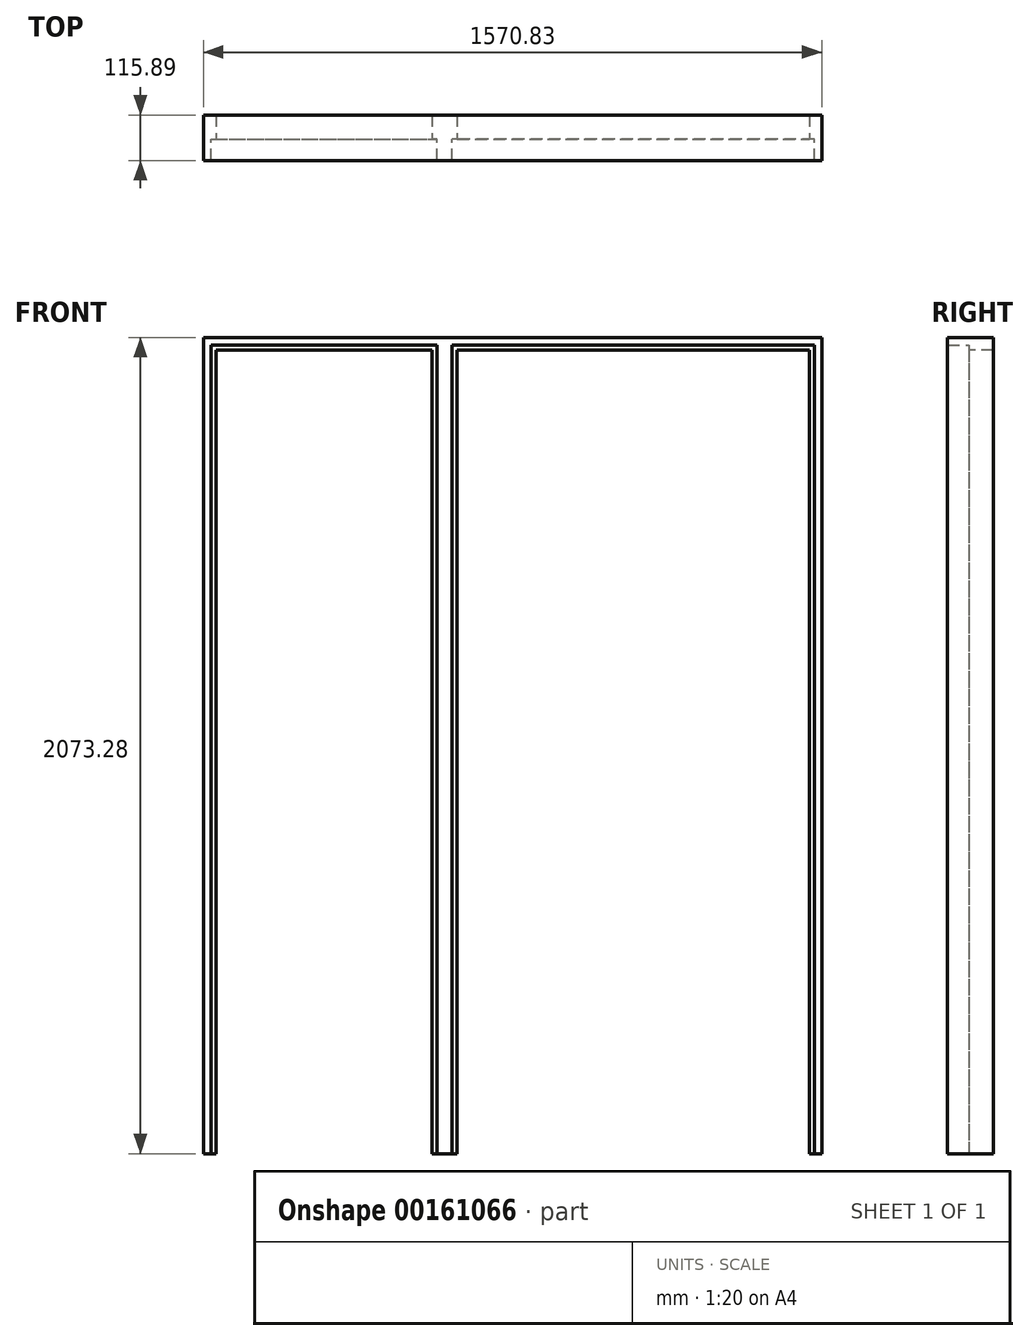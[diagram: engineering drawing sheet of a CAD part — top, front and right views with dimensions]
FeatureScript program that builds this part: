
annotation { "Feature Type Name" : "Feature", "Feature Type Description" : "" }
export const myFeature = defineFeature(function(context is Context, id is Id, definition is map)
    precondition{}
    {
        {
            var Q0;
            Q0=qCreatedBy(makeId("Front.planeOp"),FACE);
            cPlane(context, id + "F0", {"entities" : qUnion([Q0]), "cplaneType" : CPlaneType.OFFSET, "offset" : 3.17 * mm, "oppositeDirection" : true, "width" : 152.4 * mm, "height" : 152.4 * mm});
        }
        {
            var Q0;
            Q0=qCreatedBy(makeId("Front.planeOp"),FACE);
            var sketch = newSketch(context, id + "F1", { "sketchPlane" : qUnion([Q0])});
            skLineSegment(sketch, "E0.bottom", {"start": v(0, 0) * mm, "end": v(19.05, 0) * mm});
            skLineSegment(sketch, "E0.top", {"start": v(0, 2054.23) * mm, "end": v(19.05, 2054.23) * mm});
            skLineSegment(sketch, "E0.left", {"start": v(0, 0) * mm, "end": v(0, 2054.23) * mm});
            skLineSegment(sketch, "E0.right", {"start": v(19.05, 0) * mm, "end": v(19.05, 2054.23) * mm});
            skLineSegment(sketch, "E1.bottom", {"start": v(31.75, 2041.53) * mm, "end": v(19.05, 2041.53) * mm});
            skLineSegment(sketch, "E1.top", {"start": v(31.75, 0) * mm, "end": v(19.05, 0) * mm});
            skLineSegment(sketch, "E1.left", {"start": v(31.75, 2041.53) * mm, "end": v(31.75, 0) * mm});
            skLineSegment(sketch, "E1.right", {"start": v(19.05, 2041.53) * mm, "end": v(19.05, 0) * mm});
            skLineSegment(sketch, "E2.left", {"start": v(0, 2054.23) * mm, "end": v(0, 2073.28) * mm});
            skPoint(sketch, "E3.oppositeSnap0", {"position": v(9.53, 0) * mm});
            skLineSegment(sketch, "E4.left", {"start": v(19.05, 2054.23) * mm, "end": v(19.05, 2041.53) * mm});
            skLineSegment(sketch, "E5.bottom", {"start": v(612.77, 2054.23) * mm, "end": v(593.72, 2054.23) * mm});
            skLineSegment(sketch, "E5.top", {"start": v(612.78, 0) * mm, "end": v(593.73, 0) * mm});
            skLineSegment(sketch, "E5.left", {"start": v(612.77, 2054.23) * mm, "end": v(612.78, 0) * mm});
            skLineSegment(sketch, "E5.right", {"start": v(593.72, 2054.23) * mm, "end": v(593.73, 0) * mm});
            skLineSegment(sketch, "E6.bottom", {"start": v(593.73, 0) * mm, "end": v(581.03, 0) * mm});
            skLineSegment(sketch, "E6.top", {"start": v(593.72, 2041.53) * mm, "end": v(581.02, 2041.53) * mm});
            skLineSegment(sketch, "E6.left", {"start": v(593.73, 0) * mm, "end": v(593.72, 2041.53) * mm});
            skLineSegment(sketch, "E6.right", {"start": v(581.03, 0) * mm, "end": v(581.02, 2041.53) * mm});
            skLineSegment(sketch, "E7.bottom", {"start": v(612.77, 2054.23) * mm, "end": v(631.83, 2054.23) * mm});
            skLineSegment(sketch, "E7.top", {"start": v(612.78, 0) * mm, "end": v(631.83, 0) * mm});
            skLineSegment(sketch, "E7.left", {"start": v(612.77, 2054.23) * mm, "end": v(612.77, 0) * mm});
            skLineSegment(sketch, "E7.right", {"start": v(631.82, 2054.23) * mm, "end": v(631.83, 0) * mm});
            skLineSegment(sketch, "E8.bottom", {"start": v(631.83, 0) * mm, "end": v(644.53, 0) * mm});
            skLineSegment(sketch, "E8.top", {"start": v(631.82, 2041.53) * mm, "end": v(644.52, 2041.53) * mm});
            skLineSegment(sketch, "E8.left", {"start": v(631.83, 0) * mm, "end": v(631.82, 2041.53) * mm});
            skLineSegment(sketch, "E8.right", {"start": v(644.53, 0) * mm, "end": v(644.52, 2041.53) * mm});
            skLineSegment(sketch, "E9.bottom", {"start": v(1570.83, 2054.23) * mm, "end": v(1551.78, 2054.23) * mm});
            skLineSegment(sketch, "E9.top", {"start": v(1570.83, 0) * mm, "end": v(1551.78, 0) * mm});
            skLineSegment(sketch, "E9.left", {"start": v(1570.83, 2054.23) * mm, "end": v(1570.83, 0) * mm});
            skLineSegment(sketch, "E9.right", {"start": v(1551.78, 2054.23) * mm, "end": v(1551.78, 0) * mm});
            skLineSegment(sketch, "E10.left", {"start": v(1570.83, 0) * mm, "end": v(1570.83, 2054.23) * mm});
            skLineSegment(sketch, "E11.bottom", {"start": v(1551.78, 2041.53) * mm, "end": v(1539.08, 2041.53) * mm});
            skLineSegment(sketch, "E11.top", {"start": v(1551.78, 0) * mm, "end": v(1539.08, 0) * mm});
            skLineSegment(sketch, "E11.left", {"start": v(1551.78, 2041.53) * mm, "end": v(1551.78, 0) * mm});
            skLineSegment(sketch, "E11.right", {"start": v(1539.08, 2041.53) * mm, "end": v(1539.08, 0) * mm});
            skLineSegment(sketch, "E12.bottom", {"start": v(19.05, 2054.23) * mm, "end": v(593.72, 2054.23) * mm});
            skLineSegment(sketch, "E12.top", {"start": v(19.05, 2041.53) * mm, "end": v(593.72, 2041.53) * mm});
            skLineSegment(sketch, "E12.right", {"start": v(593.72, 2054.23) * mm, "end": v(593.72, 2041.53) * mm});
            skLineSegment(sketch, "E13.bottom", {"start": v(631.83, 2054.23) * mm, "end": v(1551.78, 2054.23) * mm});
            skLineSegment(sketch, "E13.top", {"start": v(631.82, 2041.53) * mm, "end": v(1551.78, 2041.53) * mm});
            skLineSegment(sketch, "E13.left", {"start": v(631.83, 2054.23) * mm, "end": v(631.83, 2041.53) * mm});
            skLineSegment(sketch, "E13.right", {"start": v(1551.78, 2054.23) * mm, "end": v(1551.78, 2041.53) * mm});
            skLineSegment(sketch, "E14", {"start": v(0, 2073.28) * mm, "end": v(1570.83, 2073.28) * mm});
            skLineSegment(sketch, "E15", {"start": v(1570.83, 2054.23) * mm, "end": v(1570.83, 2073.28) * mm});
            skSolve(sketch);
        }
        {
            var Q0;
            Q0=qCreatedBy(id+"F0.planeOp",FACE);
            var sketch = newSketch(context, id + "F2", { "sketchPlane" : qUnion([Q0])});
            skLineSegment(sketch, "E16.0", {"start": v(0, 0) * mm, "end": v(0, 2054.23) * mm});
            skLineSegment(sketch, "E17.0", {"start": v(0, 0) * mm, "end": v(19.05, 0) * mm});
            skLineSegment(sketch, "E18.0", {"start": v(31.75, 0) * mm, "end": v(19.05, 0) * mm});
            skLineSegment(sketch, "E19.0", {"start": v(31.75, 2041.53) * mm, "end": v(31.75, 0) * mm});
            skLineSegment(sketch, "E20.0", {"start": v(19.05, 2041.53) * mm, "end": v(593.72, 2041.53) * mm});
            skLineSegment(sketch, "E21.0", {"start": v(581.03, 0) * mm, "end": v(581.02, 2041.53) * mm});
            skLineSegment(sketch, "E22.0", {"start": v(0, 2054.23) * mm, "end": v(0, 2073.28) * mm});
            skLineSegment(sketch, "E23.0", {"start": v(631.82, 2041.53) * mm, "end": v(1551.78, 2041.53) * mm});
            skLineSegment(sketch, "E24.0", {"start": v(644.53, 0) * mm, "end": v(644.52, 2041.53) * mm});
            skLineSegment(sketch, "E25.0", {"start": v(1539.08, 2041.53) * mm, "end": v(1539.08, 0) * mm});
            skLineSegment(sketch, "E26.0", {"start": v(593.73, 0) * mm, "end": v(581.03, 0) * mm});
            skLineSegment(sketch, "E27.0", {"start": v(612.78, 0) * mm, "end": v(593.73, 0) * mm});
            skLineSegment(sketch, "E28.0", {"start": v(612.78, 0) * mm, "end": v(631.83, 0) * mm});
            skLineSegment(sketch, "E29.0", {"start": v(631.83, 0) * mm, "end": v(644.53, 0) * mm});
            skLineSegment(sketch, "E30.0", {"start": v(1551.78, 0) * mm, "end": v(1539.08, 0) * mm});
            skLineSegment(sketch, "E31.0", {"start": v(1570.83, 0) * mm, "end": v(1551.78, 0) * mm});
            skLineSegment(sketch, "E32", {"start": v(0, 2073.28) * mm, "end": v(1570.83, 2073.28) * mm});
            skLineSegment(sketch, "E33", {"start": v(1570.83, 2073.28) * mm, "end": v(1570.83, 0) * mm});
            skSolve(sketch);
        }
        {
            var Q0;
            Q0=qSketchRegion(id+"F2",true);
            extrude(context, id + "F3", {"entities" : qUnion([Q0]), "oppositeDirection" : true, "depth" : 61.9 * mm});
        }
        {
            var Q0;
            Q0=qCreatedBy(makeId("Front.planeOp"),FACE);
            var sketch = newSketch(context, id + "F4", { "sketchPlane" : qUnion([Q0])});
            skLineSegment(sketch, "E34.0", {"start": v(0, 0) * mm, "end": v(19.05, 0) * mm});
            skLineSegment(sketch, "E35.0", {"start": v(19.05, 2041.53) * mm, "end": v(19.05, 0) * mm});
            skLineSegment(sketch, "E36.0", {"start": v(0, 0) * mm, "end": v(0, 2054.23) * mm});
            skLineSegment(sketch, "E37.0", {"start": v(0, 2054.23) * mm, "end": v(0, 2073.28) * mm});
            skLineSegment(sketch, "E38.0", {"start": v(19.05, 2054.23) * mm, "end": v(19.05, 2041.53) * mm});
            skLineSegment(sketch, "E39.0", {"start": v(19.05, 2054.23) * mm, "end": v(593.72, 2054.23) * mm});
            skLineSegment(sketch, "E40.0", {"start": v(593.72, 2054.23) * mm, "end": v(593.73, 0) * mm});
            skLineSegment(sketch, "E41.0", {"start": v(631.82, 2054.23) * mm, "end": v(631.83, 0) * mm});
            skLineSegment(sketch, "E42.0", {"start": v(612.78, 0) * mm, "end": v(593.73, 0) * mm});
            skLineSegment(sketch, "E43.0", {"start": v(612.78, 0) * mm, "end": v(631.83, 0) * mm});
            skLineSegment(sketch, "E44.0", {"start": v(1551.78, 2054.23) * mm, "end": v(1551.78, 2041.53) * mm});
            skLineSegment(sketch, "E45.0", {"start": v(1551.78, 2041.53) * mm, "end": v(1551.78, 0) * mm});
            skLineSegment(sketch, "E46", {"start": v(1551.78, 2054.23) * mm, "end": v(631.82, 2054.23) * mm});
            skLineSegment(sketch, "E47.0", {"start": v(1570.83, 0) * mm, "end": v(1551.78, 0) * mm});
            skLineSegment(sketch, "E48", {"start": v(1570.83, 0) * mm, "end": v(1570.83, 2073.28) * mm});
            skLineSegment(sketch, "E49", {"start": v(1570.83, 2073.28) * mm, "end": v(0, 2073.28) * mm});
            skSolve(sketch);
        }
        {
            var Q0;
            Q0=qSketchRegion(id+"F4",true);
            extrude(context, id + "F5", {"entities" : qUnion([Q0]), "operationType" : NewBodyOperationType.ADD, "depth" : 50.8 * mm, "hasSecondDirection" : true, "secondDirectionOppositeDirection" : true, "secondDirectionDepth" : 3.17 * mm});
        }
    });
